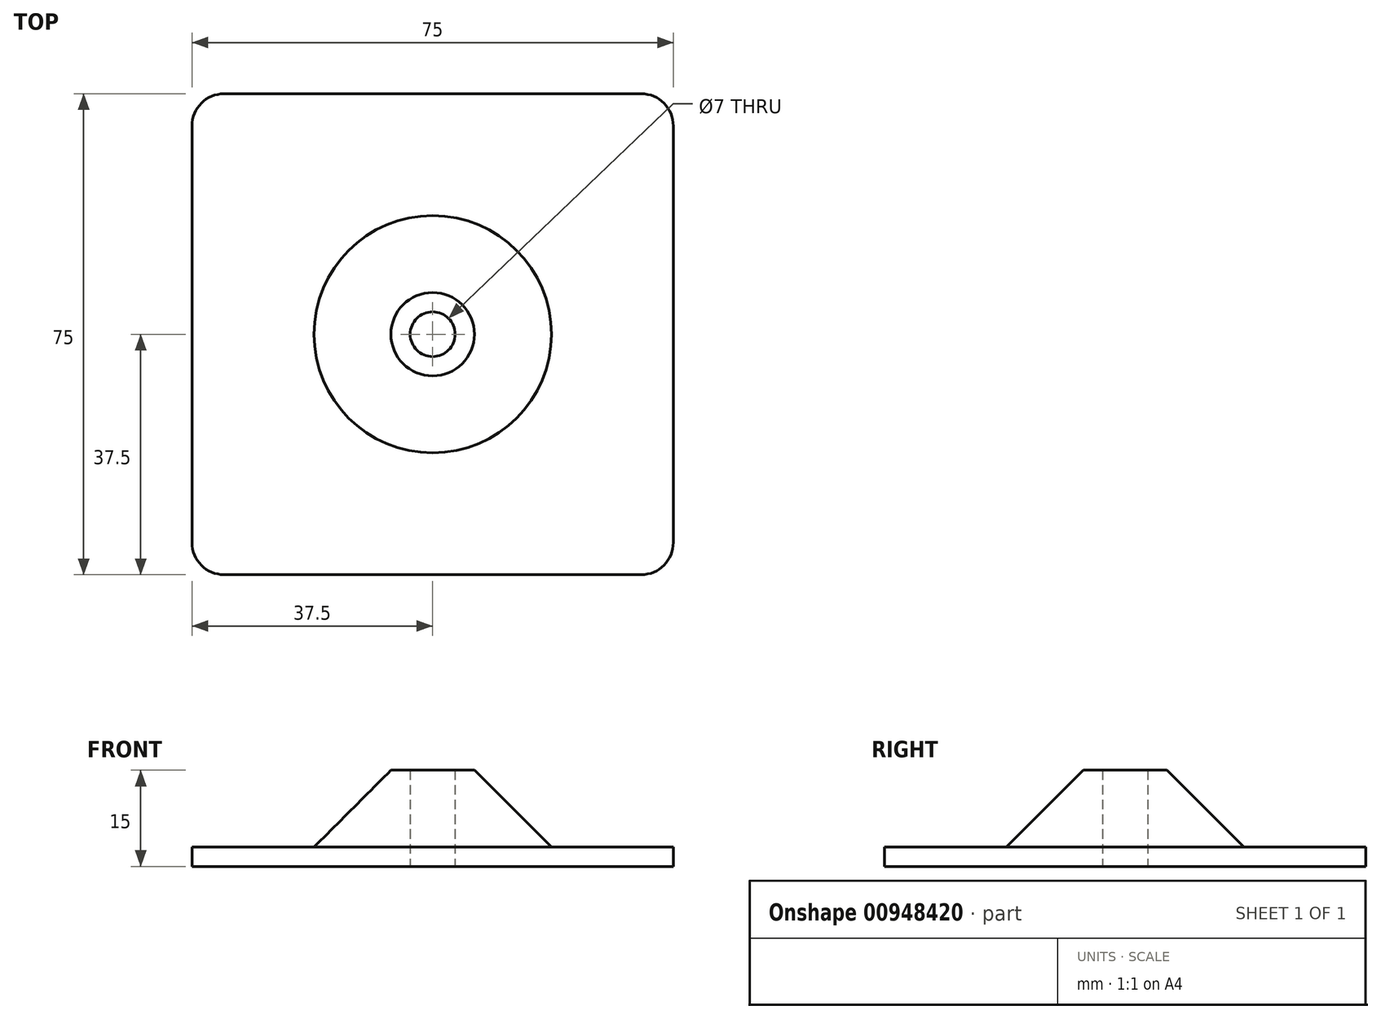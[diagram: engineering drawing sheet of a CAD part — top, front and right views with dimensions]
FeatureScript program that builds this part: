
annotation { "Feature Type Name" : "Feature", "Feature Type Description" : "" }
export const myFeature = defineFeature(function(context is Context, id is Id, definition is map)
    precondition{}
    {
        {
            var Q0;
            Q0=qCreatedBy(makeId("Top.planeOp"),FACE);
            var sketch = newSketch(context, id + "F0", { "sketchPlane" : qUnion([Q0])});
            skLineSegment(sketch, "E0.bottom", {"start": v(-37.5, -37.5) * mm, "end": v(37.5, -37.5) * mm});
            skLineSegment(sketch, "E0.top", {"start": v(-37.5, 37.5) * mm, "end": v(37.5, 37.5) * mm});
            skLineSegment(sketch, "E0.left", {"start": v(-37.5, -37.5) * mm, "end": v(-37.5, 37.5) * mm});
            skLineSegment(sketch, "E0.right", {"start": v(37.5, -37.5) * mm, "end": v(37.5, 37.5) * mm});
            skLineSegment(sketch, "E1", {"start": v(-37.5, -37.5) * mm, "end": v(37.5, 37.5) * mm, "construction": true});
            skSolve(sketch);
        }
        {
            var Q0;
            Q0 = qSketchRegion(id + "F0", true);
            extrude(context, id + "F1", {"entities" : qUnion([Q0]), "depth" : 3 * mm, "offsetDistance" : 25 * mm});
        }
        {
            var Q0;
            Q0=qCreatedBy(makeId("Front.planeOp"),FACE);
            var sketch = newSketch(context, id + "F2", { "sketchPlane" : qUnion([Q0])});
            skLineSegment(sketch, "E2", {"start": v(0, 0) * mm, "end": v(0, 56.51) * mm, "construction": true});
            skPoint(sketch, "E3.0", {"position": v(-37.5, 3) * mm});
            skLineSegment(sketch, "E4", {"start": v(-18.5, 3) * mm, "end": v(-6.5, 15) * mm});
            skLineSegment(sketch, "E5", {"start": v(-6.5, 15) * mm, "end": v(-3.5, 15) * mm});
            skLineSegment(sketch, "E6", {"start": v(-3.5, 15) * mm, "end": v(-3.5, 3) * mm});
            skLineSegment(sketch, "E7", {"start": v(-3.5, 3) * mm, "end": v(-18.5, 3) * mm});
            skSolve(sketch);
        }
        {
            var Q0;
            Q0 = qSketchRegion(id + "F2", true);
            var Q1;
            Q1=sQuery(id+"F2.wireOp",EDGE,"E2");
            revolve(context, id + "F3", {"operationType" : NewBodyOperationType.ADD, "surfaceOperationType" : NewSurfaceOperationType.NEW, "entities" : qUnion([Q0]), "axis" : qUnion([Q1]), "revolveType" : RevolveType.FULL});
        }
        {
            var Q0;
            Q0=makeQuery(id+"F3.opRevolve","SWEPT_FACE",FACE,{"disambiguationData":[OSD([sQuery(id+"F2.wireOp",EDGE,"E5")])]});
            var sketch = newSketch(context, id + "F4", { "sketchPlane" : qUnion([Q0])});
            skCircle(sketch, "E8.0", {"center": v(0, 0) * mm, "radius": 3.5 * mm});
            skSolve(sketch);
        }
        {
            var Q0;
            Q0 = qSketchRegion(id + "F4", true);
            extrude(context, id + "F5", {"entities" : qUnion([Q0]), "operationType" : NewBodyOperationType.REMOVE, "endBound" : BoundingType.THROUGH_ALL, "oppositeDirection" : true, "depth" : 25 * mm, "offsetDistance" : 25 * mm});
        }
        {
            var Q0;
            Q0=makeQuery(id+"F1.opExtrude","SWEPT_EDGE",EDGE,{"disambiguationData":[OSD([sQuery(id+"F0.wireOp",EDGE,"E0.top"),sQuery(id+"F0.wireOp",EDGE,"E0.left")])]});
            var Q1;
            Q1=makeQuery(id+"F1.opExtrude","SWEPT_EDGE",EDGE,{"disambiguationData":[OSD([sQuery(id+"F0.wireOp",EDGE,"E0.bottom"),sQuery(id+"F0.wireOp",EDGE,"E0.left")])]});
            var Q2;
            Q2=makeQuery(id+"F1.opExtrude","SWEPT_EDGE",EDGE,{"disambiguationData":[OSD([sQuery(id+"F0.wireOp",EDGE,"E0.bottom"),sQuery(id+"F0.wireOp",EDGE,"E0.right")])]});
            var Q3;
            Q3=makeQuery(id+"F1.opExtrude","SWEPT_EDGE",EDGE,{"disambiguationData":[OSD([sQuery(id+"F0.wireOp",EDGE,"E0.top"),sQuery(id+"F0.wireOp",EDGE,"E0.right")])]});
            fillet(context, id + "F6", {"entities" : qUnion([Q0, Q1, Q2, Q3]), "radius" : 5 * mm, "tangentPropagation" : true, "allowEdgeOverflow" : false});
        }
    });
